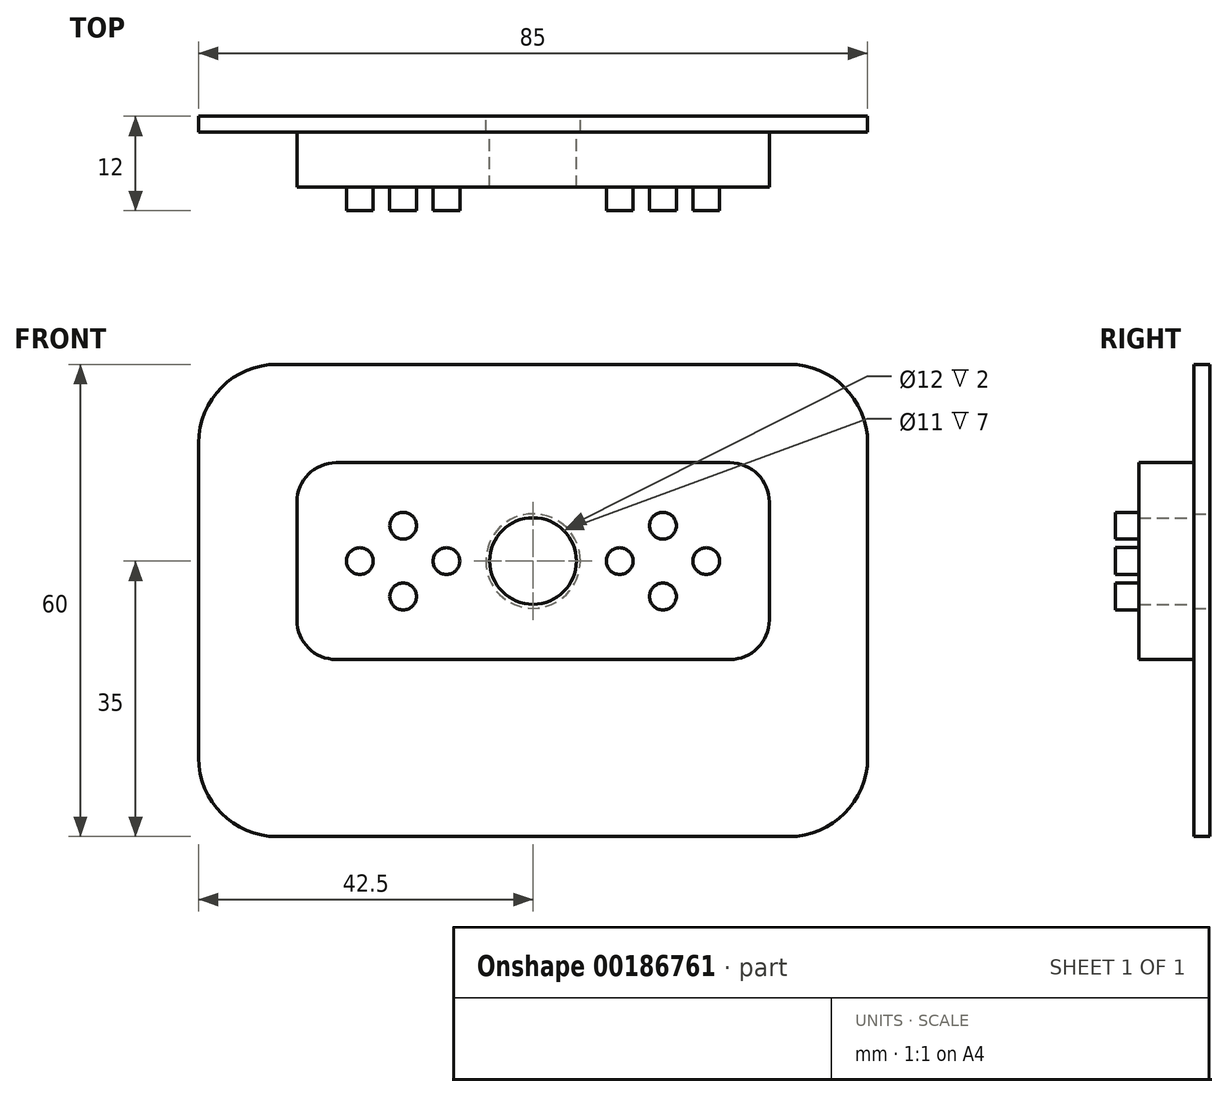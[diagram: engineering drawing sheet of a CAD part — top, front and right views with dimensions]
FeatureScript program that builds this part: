
annotation { "Feature Type Name" : "Feature", "Feature Type Description" : "" }
export const myFeature = defineFeature(function(context is Context, id is Id, definition is map)
    precondition{}
    {
        {
            var Q0;
            Q0=qCreatedBy(makeId("Front.planeOp"),FACE);
            var sketch = newSketch(context, id + "F0", { "sketchPlane" : qUnion([Q0])});
            skLineSegment(sketch, "E0.bottom", {"start": v(42.5, -35) * mm, "end": v(-42.5, -35) * mm});
            skLineSegment(sketch, "E0.top", {"start": v(42.5, 25) * mm, "end": v(-42.5, 25) * mm});
            skLineSegment(sketch, "E0.left", {"start": v(42.5, -35) * mm, "end": v(42.5, 25) * mm});
            skLineSegment(sketch, "E0.right", {"start": v(-42.5, -35) * mm, "end": v(-42.5, 25) * mm});
            skCircle(sketch, "E1", {"center": v(0, 0) * mm, "radius": 6 * mm});
            skSolve(sketch);
        }
        {
            var Q0;
            Q0=qSketchRegion(id+"F0",true);
            extrude(context, id + "F1", {"entities" : qUnion([Q0]), "depth" : 2 * mm});
        }
        {
            var Q0;
            Q0=makeQuery(id+"F1.opExtrude","CAP_FACE",FACE,{"disambiguationData":[OSD([sQuery(id+"F0.wireOp",EDGE,"E0.bottom"),sQuery(id+"F0.wireOp",EDGE,"E0.top"),sQuery(id+"F0.wireOp",EDGE,"E0.left"),sQuery(id+"F0.wireOp",EDGE,"E0.right"),sQuery(id+"F0.wireOp",EDGE,"E1")])],"isStart":false});
            var sketch = newSketch(context, id + "F2", { "sketchPlane" : qUnion([Q0])});
            skLineSegment(sketch, "E2.bottom", {"start": v(-30, 12.5) * mm, "end": v(30, 12.5) * mm});
            skLineSegment(sketch, "E2.top", {"start": v(-30, -12.5) * mm, "end": v(30, -12.5) * mm});
            skLineSegment(sketch, "E2.left", {"start": v(-30, 12.5) * mm, "end": v(-30, -12.5) * mm});
            skLineSegment(sketch, "E2.right", {"start": v(30, 12.5) * mm, "end": v(30, -12.5) * mm});
            skPoint(sketch, "E2.middle", {"position": v(0, 0) * mm});
            skCircle(sketch, "E3", {"center": v(0, 0) * mm, "radius": 5.5 * mm});
            skSolve(sketch);
        }
        {
            var Q0;
            Q0=qSketchRegion(id+"F2",true);
            extrude(context, id + "F3", {"entities" : qUnion([Q0]), "operationType" : NewBodyOperationType.ADD, "depth" : 7 * mm});
        }
        {
            var Q0;
            Q0=makeQuery(id+"F3.opExtrude","SWEPT_EDGE",EDGE,{"disambiguationData":[OSD([sQuery(id+"F2.wireOp",EDGE,"E2.bottom"),sQuery(id+"F2.wireOp",EDGE,"E2.right")])]});
            var Q1;
            Q1=makeQuery(id+"F3.opExtrude","SWEPT_EDGE",EDGE,{"disambiguationData":[OSD([sQuery(id+"F2.wireOp",EDGE,"E2.top"),sQuery(id+"F2.wireOp",EDGE,"E2.right")])]});
            var Q2;
            Q2=makeQuery(id+"F3.opExtrude","SWEPT_EDGE",EDGE,{"disambiguationData":[OSD([sQuery(id+"F2.wireOp",EDGE,"E2.top"),sQuery(id+"F2.wireOp",EDGE,"E2.left")])]});
            var Q3;
            Q3=makeQuery(id+"F3.opExtrude","SWEPT_EDGE",EDGE,{"disambiguationData":[OSD([sQuery(id+"F2.wireOp",EDGE,"E2.bottom"),sQuery(id+"F2.wireOp",EDGE,"E2.left")])]});
            fillet(context, id + "F4", {"entities" : qUnion([Q0, Q1, Q2, Q3]), "radius" : 5 * mm, "tangentPropagation" : true, "allowEdgeOverflow" : false});
        }
        {
            var Q0;
            Q0=makeQuery(id+"F1.opExtrude","SWEPT_EDGE",EDGE,{"disambiguationData":[OSD([sQuery(id+"F0.wireOp",EDGE,"E0.top"),sQuery(id+"F0.wireOp",EDGE,"E0.left")])]});
            var Q1;
            Q1=makeQuery(id+"F1.opExtrude","SWEPT_EDGE",EDGE,{"disambiguationData":[OSD([sQuery(id+"F0.wireOp",EDGE,"E0.bottom"),sQuery(id+"F0.wireOp",EDGE,"E0.left")])]});
            var Q2;
            Q2=makeQuery(id+"F1.opExtrude","SWEPT_EDGE",EDGE,{"disambiguationData":[OSD([sQuery(id+"F0.wireOp",EDGE,"E0.bottom"),sQuery(id+"F0.wireOp",EDGE,"E0.right")])]});
            var Q3;
            Q3=makeQuery(id+"F1.opExtrude","SWEPT_EDGE",EDGE,{"disambiguationData":[OSD([sQuery(id+"F0.wireOp",EDGE,"E0.top"),sQuery(id+"F0.wireOp",EDGE,"E0.right")])]});
            fillet(context, id + "F5", {"entities" : qUnion([Q0, Q1, Q2, Q3]), "radius" : 10 * mm, "tangentPropagation" : true, "allowEdgeOverflow" : false});
        }
        {
            var Q0;
            Q0=makeQuery(id+"F3.opExtrude","CAP_FACE",FACE,{"disambiguationData":[OSD([sQuery(id+"F2.wireOp",EDGE,"E2.bottom"),sQuery(id+"F2.wireOp",EDGE,"E2.top"),sQuery(id+"F2.wireOp",EDGE,"E2.left"),sQuery(id+"F2.wireOp",EDGE,"E2.right"),sQuery(id+"F2.wireOp",EDGE,"E3")])],"isStart":false});
            var sketch = newSketch(context, id + "F6", { "sketchPlane" : qUnion([Q0])});
            skCircle(sketch, "E4", {"center": v(-11, 0) * mm, "radius": 1.7 * mm});
            skCircle(sketch, "E5", {"center": v(-22, 0) * mm, "radius": 1.7 * mm});
            skCircle(sketch, "E6", {"center": v(11, 0) * mm, "radius": 1.7 * mm});
            skCircle(sketch, "E7", {"center": v(22, 0) * mm, "radius": 1.7 * mm});
            skCircle(sketch, "E8", {"center": v(-16.5, -4.5) * mm, "radius": 1.7 * mm});
            skCircle(sketch, "E9", {"center": v(16.5, -4.5) * mm, "radius": 1.7 * mm});
            skCircle(sketch, "E10", {"center": v(16.5, 4.5) * mm, "radius": 1.7 * mm});
            skCircle(sketch, "E11", {"center": v(-16.5, 4.5) * mm, "radius": 1.7 * mm});
            skSolve(sketch);
        }
        {
            var Q0;
            Q0=qSketchRegion(id+"F6",true);
            extrude(context, id + "F7", {"entities" : qUnion([Q0]), "operationType" : NewBodyOperationType.ADD, "depth" : 3 * mm});
        }
    });
